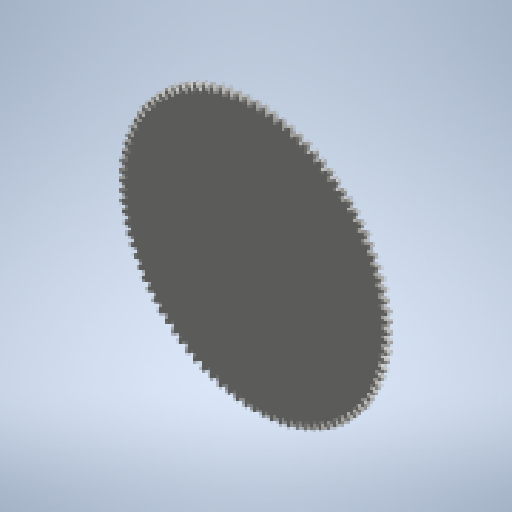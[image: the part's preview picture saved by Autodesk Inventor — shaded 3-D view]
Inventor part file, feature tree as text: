
AUTODESK INVENTOR PART (.ipt)
format: ipt  version: 2025 (Build 290162010, 162A)  size: 565,248 bytes
history: native  units: mm (DEFAULTED — no unit token found)
features: plane x3, other x3, extrude x1, sketch x1
ambient origin geometry x8: Origin, YZ Plane, XZ Plane, XY Plane, X Axis, Y Axis, Z Axis, Center Point
bodies: Solid1 (feature_tree)
feature tree (8):
  extrude  "Extrusion1"  Depth=20.0mm TaperAngle=0.0deg
  plane  "Work Plane2"
  plane  "Work Plane8"
  plane  "Work Plane9"
  other  "Spur Gear"
  sketch  "Sketch1"  dims[d0=1425.0mm d1=20.0mm d2=0.0mm d3=1400.0mm d4=10.0mm d5=0.0mm d16=800.0mm d17=0.0mm d34=0.280499mm d39=0.0mm d41=0.0mm d43=800.0mm d46=800.0mm d47=0.0mm d48=0.0mm]
  other  "Srf1"
  other  "Pitch Diameter"
